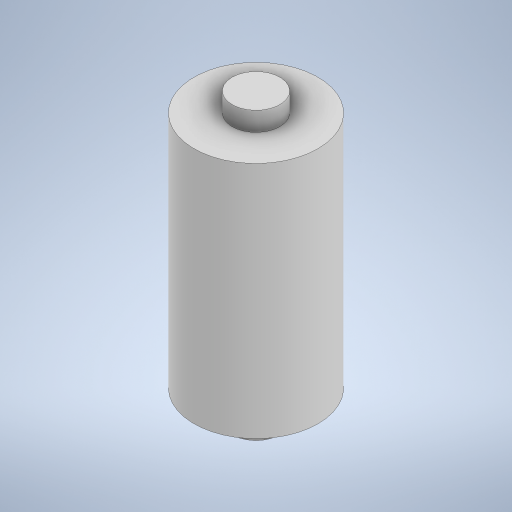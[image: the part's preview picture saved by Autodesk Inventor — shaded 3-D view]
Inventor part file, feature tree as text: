
AUTODESK INVENTOR PART (.ipt)
format: ipt  version: 2023 (Build 270158000, 158)  size: 227,328 bytes
history: native  units: in
note: dims shown in document units (in); Inventor stores cm internally (conversion verified against a paired STEP export)
features: extrude x2, sketch x2, plane x1
ambient origin geometry x8: Origin, YZ Plane, XZ Plane, XY Plane, X Axis, Y Axis, Z Axis, Center Point
bodies: Solid1 (feature_tree)
feature tree (5):
  extrude  "Extrusion1"  Depth=1.1811in TaperAngle=0.0deg
  plane  "Work Plane1"
  extrude  "Extrusion2"  Depth=0.9843in
  sketch  "Sketch1"  dims[d0=0.1969in d1=1.1811in d2=0.0in]
  sketch  "Sketch2"  dims[d3=-0.1181in d4=0.5118in d5=0.9843in d6=0.0in]
